# Revit family: Plumbing_Other-Plumbing_Menzies-Metal_Plumbing-Stack-Spun-Aluminum-TPO
name_source: partatom
category: Plumbing Fixtures
revit_build: Autodesk Revit 2018 (Build: 20170223_1515(x64)
units: mm (PartAtom-declared; Revit-internal decimal feet)

## family parameters
Cut with Voids When Loaded = No
Host = Face
OmniClass Number = 23.70.50.21.24.11
OmniClass Title = Roof Waste Water Drains
Part Type = Normal
Room Calculation Point = No
Round Connector Dimension = Use Diameter
Shared = No

## types (5) — shared parameters
Assembly Code = D2040200
CW Connection = No
Default Elevation = 4' - 0"
Description = Plumbing Stack Spun Aluminum-TPO
Drain Flow = 0 GPM
Edition number = 1
HW Connection = No
Manufacturer = Menzies Metal Products
Pipe Length = 1' - 0"
Product Guid = 02c721fd-952f-48cd-9394-e694986ec419
Product Material = Metal - Menzies Metal Products - Aluminium TPO Coated
Product data url = https://www.bimobject.com
URL = https://www.menzies-metal.com
Vent Connection = Yes
Waste Connection = No

## per-type parameters (varying)
| type | Model | Pipe Diameter | Weight |
| 2" | 400-4315TPO | 2" | 0.80 lbf |
| 3" | 400-4320TPO | 3" | 1.10 lbf |
| 4" | 400-4325TPO | 4" | 1.30 lbf |
| 1.5" | 400-4310TPO | 2" | 0.75 lbf |
| 5" | 400-4330TPO | 5" | 1.50 lbf |

## geometry (parser evidence)
native form markers: Sweep x4
no freeform markers — native parametric forms only
